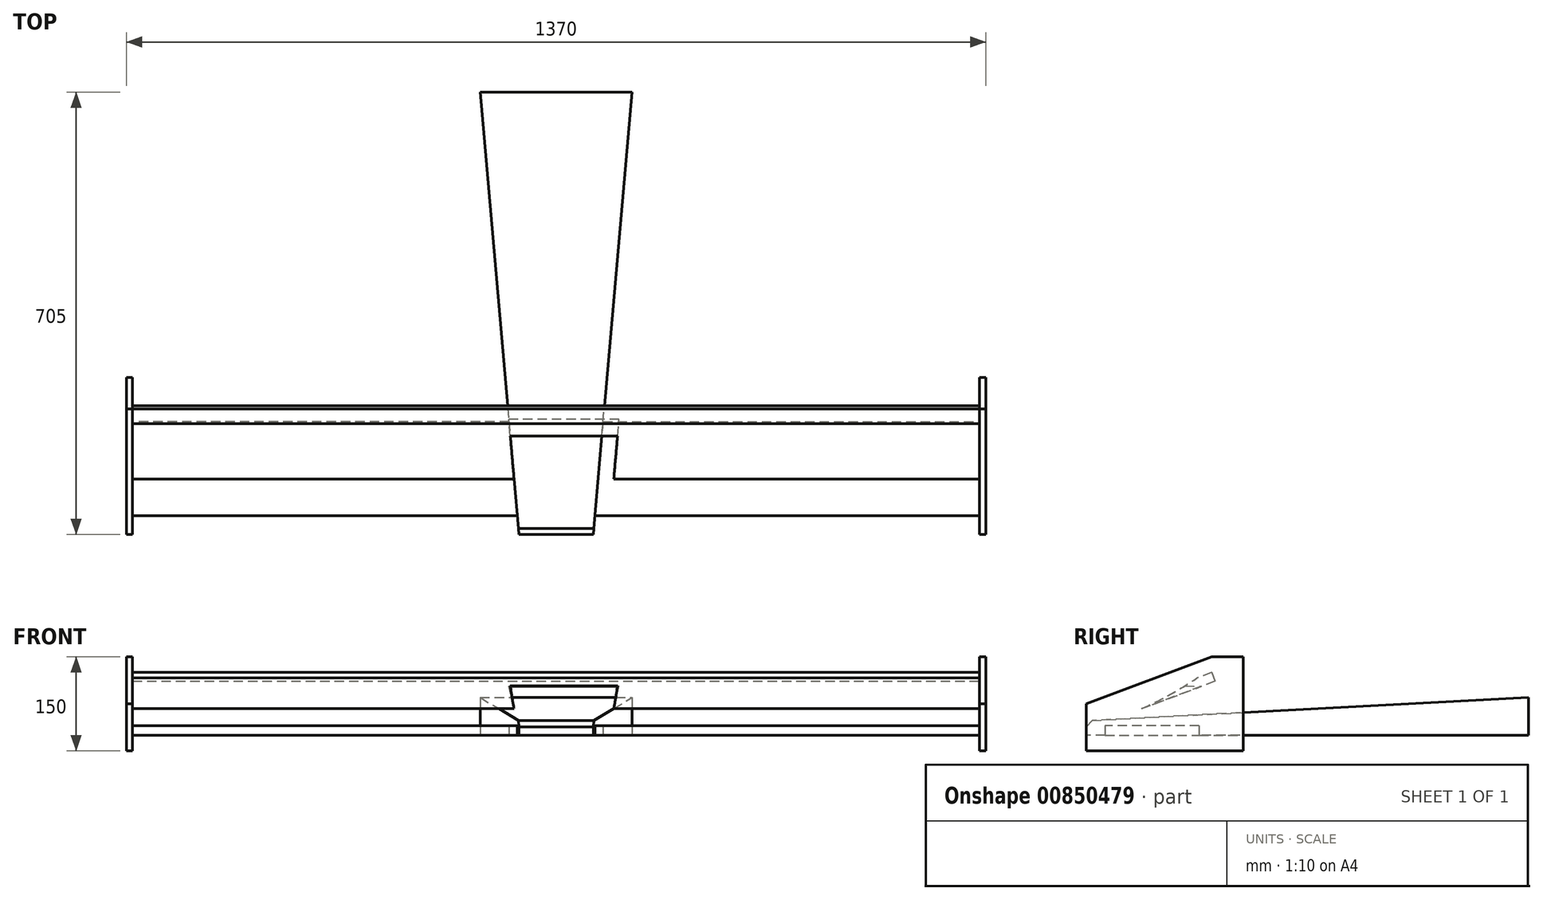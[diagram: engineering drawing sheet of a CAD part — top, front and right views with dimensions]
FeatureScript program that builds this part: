
annotation { "Feature Type Name" : "Feature", "Feature Type Description" : "" }
export const myFeature = defineFeature(function(context is Context, id is Id, definition is map)
    precondition{}
    {
        {
            var Q0;
            Q0=qCreatedBy(makeId("Top.planeOp"),FACE);
            var sketch = newSketch(context, id + "F0", { "sketchPlane" : qUnion([Q0])});
            skLineSegment(sketch, "E0", {"start": v(0, 0) * mm, "end": v(0, -525) * mm});
            skLineSegment(sketch, "E1", {"start": v(0, -525) * mm, "end": v(75, -525) * mm});
            skLineSegment(sketch, "E2", {"start": v(75, -525) * mm, "end": v(120.93, 0) * mm});
            skLineSegment(sketch, "E3", {"start": v(120.93, 0) * mm, "end": v(0, 0) * mm});
            skLineSegment(sketch, "E4", {"start": v(675, -675) * mm, "end": v(675, -525) * mm});
            skLineSegment(sketch, "E5", {"start": v(75, -525) * mm, "end": v(675, -525) * mm});
            skLineSegment(sketch, "E6", {"start": v(120.93, 0) * mm, "end": v(119.04, -21.63) * mm});
            skLineSegment(sketch, "E7", {"start": v(75, -525) * mm, "end": v(59.25, -705) * mm});
            skLineSegment(sketch, "E8", {"start": v(0, -525) * mm, "end": v(0, -705) * mm});
            skLineSegment(sketch, "E9", {"start": v(675, -675) * mm, "end": v(61.88, -675) * mm});
            skPoint(sketch, "E10", {"position": v(0, -675) * mm});
            skLineSegment(sketch, "E11", {"start": v(0, -705) * mm, "end": v(59.25, -705) * mm});
            skLineSegment(sketch, "E12", {"start": v(0, -877.72) * mm, "end": v(0, 311.7) * mm, "construction": true});
            skLineSegment(sketch, "E13.MirrorCS", {"start": v(-120.93, 0) * mm, "end": v(-119.04, -21.63) * mm});
            skLineSegment(sketch, "E14.MirrorCS", {"start": v(0, -705) * mm, "end": v(-59.25, -705) * mm});
            skLineSegment(sketch, "E15.MirrorCS", {"start": v(-75, -525) * mm, "end": v(-120.93, 0) * mm});
            skLineSegment(sketch, "E16.MirrorCS", {"start": v(-675, -675) * mm, "end": v(-61.88, -675) * mm});
            skLineSegment(sketch, "E17.MirrorCS", {"start": v(-75, -525) * mm, "end": v(-59.25, -705) * mm});
            skLineSegment(sketch, "E18.MirrorCS", {"start": v(0, -525) * mm, "end": v(-75, -525) * mm});
            skLineSegment(sketch, "E19.MirrorCS", {"start": v(-75, -525) * mm, "end": v(-675, -525) * mm});
            skLineSegment(sketch, "E20.MirrorCS", {"start": v(-120.93, 0) * mm, "end": v(0, 0) * mm});
            skLineSegment(sketch, "E21.MirrorCS", {"start": v(-675, -675) * mm, "end": v(-675, -525) * mm});
            skSolve(sketch);
        }
        {
            var Q0;
            {var subQ0=sQuery(id+"F0.wireOp",EDGE,"E16.MirrorCS");Q0=makeQuery(id+"F0.imprint","IMPRINT",FACE,{"disambiguationData":[TD([[makeQuery(id+"F0.imprint","IMPRINT",EDGE,{"derivedFrom":subQ0}),1.0]])]});}
            var Q1;
            {var subQ0=sQuery(id+"F0.wireOp",EDGE,"E18.MirrorCS");Q1=makeQuery(id+"F0.imprint","IMPRINT",FACE,{"disambiguationData":[TD([[makeQuery(id+"F0.imprint","IMPRINT",EDGE,{"derivedFrom":subQ0}),-1.0]])]});}
            var Q2;
            Q2=makeQuery(id+"F0.imprint","IMPRINT",FACE,{"disambiguationData":[TD([[makeQuery(id+"F0.imprint","IMPRINT",EDGE,{"derivedFrom":sQuery(id+"F0.wireOp",EDGE,"E1")}),1.0]])]});
            var Q3;
            {var subQ3=sQuery(id+"F0.wireOp",EDGE,"E14.MirrorCS");Q3=makeQuery(id+"F0.imprint","IMPRINT",FACE,{"disambiguationData":[TD([[makeQuery(id+"F0.imprint","IMPRINT",EDGE,{"derivedFrom":subQ3}),-1.0]])]});}
            var Q4;
            {var subQ3=sQuery(id+"F0.wireOp",EDGE,"E1");Q4=makeQuery(id+"F0.imprint","IMPRINT",FACE,{"disambiguationData":[TD([[makeQuery(id+"F0.imprint","IMPRINT",EDGE,{"derivedFrom":subQ3}),-1.0]])]});}
            var Q5;
            Q5=makeQuery(id+"F0.imprint","IMPRINT",FACE,{"disambiguationData":[TD([[makeQuery(id+"F0.imprint","IMPRINT",EDGE,{"derivedFrom":sQuery(id+"F0.wireOp",EDGE,"E4")}),1.0]])]});
            extrude(context, id + "F1", {"entities" : qUnion([Q0, Q1, Q2, Q3, Q4, Q5]), "depth" : 15 * mm, "offsetDistance" : 25 * mm});
        }
        {
            var Q0;
            Q0=makeQuery(id+"F1.opExtrude","SWEPT_FACE",FACE,{"disambiguationData":[OSD([sQuery(id+"F0.wireOp",EDGE,"E4")])]});
            var sketch = newSketch(context, id + "F2", { "sketchPlane" : qUnion([Q0])});
            skLineSegment(sketch, "E22.bottom", {"start": v(-675, 15) * mm, "end": v(-525, 15) * mm});
            skLineSegment(sketch, "E22.top", {"start": v(-675, 0) * mm, "end": v(-525, 0) * mm});
            skLineSegment(sketch, "E22.left", {"start": v(-675, 15) * mm, "end": v(-675, 0) * mm});
            skLineSegment(sketch, "E22.right", {"start": v(-525, 15) * mm, "end": v(-525, 0) * mm});
            skLineSegment(sketch, "E23", {"start": v(-705, 0) * mm, "end": v(-705, 50) * mm});
            skLineSegment(sketch, "E24", {"start": v(-705, 0) * mm, "end": v(-705, -25) * mm});
            skLineSegment(sketch, "E25", {"start": v(-705, -25) * mm, "end": v(-455, -25) * mm});
            skLineSegment(sketch, "E26", {"start": v(-455, -25) * mm, "end": v(-455, 125) * mm});
            skLineSegment(sketch, "E27", {"start": v(-455, 125) * mm, "end": v(-505, 125) * mm});
            skLineSegment(sketch, "E28", {"start": v(-705, 50) * mm, "end": v(-505, 125) * mm});
            skLineSegment(sketch, "E29.bottom", {"start": v(-705, 50) * mm, "end": v(-455, 50) * mm});
            skLineSegment(sketch, "E29.left", {"start": v(-705, 50) * mm, "end": v(-705, -25) * mm});
            skLineSegment(sketch, "E29.right", {"start": v(-455, 50) * mm, "end": v(-455, -25) * mm});
            skSolve(sketch);
        }
        {
            var Q0;
            Q0=makeQuery(id+"F2.imprint","IMPRINT",FACE,{"disambiguationData":[TD([[makeQuery(id+"F2.imprint","IMPRINT",EDGE,{"derivedFrom":sQuery(id+"F2.wireOp",EDGE,"E26")}),1.0]])]});
            var Q1;
            Q1=makeQuery(id+"F2.imprint","IMPRINT",FACE,{"disambiguationData":[TD([[makeQuery(id+"F2.imprint","IMPRINT",EDGE,{"derivedFrom":sQuery(id+"F2.wireOp",EDGE,"E22.bottom")}),1.0]])]});
            var Q2;
            Q2=makeQuery(id+"F2.imprint","IMPRINT",FACE,{"disambiguationData":[TD([[makeQuery(id+"F2.imprint","IMPRINT",EDGE,{"derivedFrom":sQuery(id+"F2.wireOp",EDGE,"E22.bottom")}),-1.0]])]});
            extrude(context, id + "F3", {"entities" : qUnion([Q0, Q1, Q2]), "operationType" : NewBodyOperationType.ADD, "depth" : 10 * mm, "offsetDistance" : 25 * mm});
        }
        {
            var Q0;
            Q0=makeQuery(id+"F1.opExtrude","SWEPT_FACE",FACE,{"disambiguationData":[OSD([sQuery(id+"F0.wireOp",EDGE,"E21.MirrorCS")])]});
            var sketch = newSketch(context, id + "F4", { "sketchPlane" : qUnion([Q0])});
            skLineSegment(sketch, "E30.bottom", {"start": v(525, 15) * mm, "end": v(675, 15) * mm});
            skLineSegment(sketch, "E30.top", {"start": v(525, 0) * mm, "end": v(675, 0) * mm});
            skLineSegment(sketch, "E30.left", {"start": v(525, 15) * mm, "end": v(525, 0) * mm});
            skLineSegment(sketch, "E30.right", {"start": v(675, 15) * mm, "end": v(675, 0) * mm});
            skLineSegment(sketch, "E31.bottom", {"start": v(455, 50) * mm, "end": v(705, 50) * mm});
            skLineSegment(sketch, "E31.top", {"start": v(455, -25) * mm, "end": v(705, -25) * mm});
            skLineSegment(sketch, "E31.left", {"start": v(455, 50) * mm, "end": v(455, -25) * mm});
            skLineSegment(sketch, "E31.right", {"start": v(705, 50) * mm, "end": v(705, -25) * mm});
            skLineSegment(sketch, "E32", {"start": v(455, 50) * mm, "end": v(455, 125) * mm});
            skLineSegment(sketch, "E33", {"start": v(455, 125) * mm, "end": v(505, 125) * mm});
            skLineSegment(sketch, "E34", {"start": v(705, 50) * mm, "end": v(505, 125) * mm});
            skSolve(sketch);
        }
        {
            var Q0;
            Q0 = qSketchRegion(id + "F4", true);
            var Q1;
            Q1=makeQuery(id+"F4.imprint","IMPRINT",FACE,{"disambiguationData":[TD([[makeQuery(id+"F4.imprint","IMPRINT",EDGE,{"derivedFrom":sQuery(id+"F4.wireOp",EDGE,"E30.bottom")}),1.0]])]});
            extrude(context, id + "F5", {"entities" : qUnion([Q0, Q1]), "depth" : 10 * mm, "offsetDistance" : 25 * mm});
        }
        {
            var Q0;
            Q0=makeQuery(id+"F1.opExtrude","CAP_FACE",FACE,{"disambiguationData":[OSD([sQuery(id+"F0.wireOp",EDGE,"E2"),sQuery(id+"F0.wireOp",EDGE,"E3"),sQuery(id+"F0.wireOp",EDGE,"E4"),sQuery(id+"F0.wireOp",EDGE,"E5"),sQuery(id+"F0.wireOp",EDGE,"E6"),sQuery(id+"F0.wireOp",EDGE,"E7"),sQuery(id+"F0.wireOp",EDGE,"E9"),sQuery(id+"F0.wireOp",EDGE,"E11"),sQuery(id+"F0.wireOp",EDGE,"E14.MirrorCS"),sQuery(id+"F0.wireOp",EDGE,"E15.MirrorCS"),sQuery(id+"F0.wireOp",EDGE,"E16.MirrorCS"),sQuery(id+"F0.wireOp",EDGE,"E17.MirrorCS"),sQuery(id+"F0.wireOp",EDGE,"E19.MirrorCS"),sQuery(id+"F0.wireOp",EDGE,"E20.MirrorCS"),sQuery(id+"F0.wireOp",EDGE,"E21.MirrorCS")])],"isStart":false});
            var sketch = newSketch(context, id + "F6", { "sketchPlane" : qUnion([Q0])});
            skLineSegment(sketch, "E35", {"start": v(-120.93, 0) * mm, "end": v(-59.25, -705) * mm});
            skLineSegment(sketch, "E36", {"start": v(-59.25, -705) * mm, "end": v(59.25, -705) * mm});
            skLineSegment(sketch, "E37", {"start": v(59.25, -705) * mm, "end": v(120.93, 0) * mm});
            skLineSegment(sketch, "E38", {"start": v(120.93, 0) * mm, "end": v(-120.93, 0) * mm});
            skSolve(sketch);
        }
        {
            var Q0;
            Q0 = qSketchRegion(id + "F6", true);
            extrude(context, id + "F7", {"entities" : qUnion([Q0]), "operationType" : NewBodyOperationType.ADD, "depth" : 45 * mm, "offsetDistance" : 25 * mm});
        }
        {
            var Q0;
            Q0=makeQuery(id+"F3.opExtrude","CAP_FACE",FACE,{"disambiguationData":[OSD([sQuery(id+"F2.wireOp",EDGE,"E26"),sQuery(id+"F2.wireOp",EDGE,"E27"),sQuery(id+"F2.wireOp",EDGE,"E28"),sQuery(id+"F2.wireOp",EDGE,"E25"),sQuery(id+"F2.wireOp",EDGE,"E29.left"),sQuery(id+"F2.wireOp",EDGE,"E29.right")])],"isStart":true});
            var sketch = newSketch(context, id + "F8", { "sketchPlane" : qUnion([Q0])});
            skLineSegment(sketch, "E39.bottom", {"start": v(455, 125) * mm, "end": v(705, 125) * mm, "construction": true});
            skLineSegment(sketch, "E39.top", {"start": v(455, -25) * mm, "end": v(705, -25) * mm, "construction": true});
            skLineSegment(sketch, "E39.left", {"start": v(455, 125) * mm, "end": v(455, -25) * mm, "construction": true});
            skLineSegment(sketch, "E39.right", {"start": v(705, 125) * mm, "end": v(705, -25) * mm, "construction": true});
            skLineSegment(sketch, "E40", {"start": v(505, 100.14) * mm, "end": v(528.4, 91.36) * mm});
            skLineSegment(sketch, "E41", {"start": v(505, 125) * mm, "end": v(705, 50) * mm, "construction": true});
            skLineSegment(sketch, "E42", {"start": v(505, 100.14) * mm, "end": v(499.73, 86.1) * mm});
            skLineSegment(sketch, "E43", {"start": v(499.73, 86.1) * mm, "end": v(616.77, 42.2) * mm});
            skArc(sketch, "E44", {"start": v(528.4, 91.36) * mm, "mid": v(571.55, 64.92) * mm, "end": v(616.77, 42.2) * mm});
            skSolve(sketch);
        }
        {
            var Q0;
            Q0=makeQuery(id+"F8.imprint","IMPRINT",FACE,{"disambiguationData":[TD([[makeQuery(id+"F8.imprint","IMPRINT",EDGE,{"derivedFrom":sQuery(id+"F8.wireOp",EDGE,"E42")}),1.0]])]});
            var Q1;
            Q1=makeQuery(id+"F5.opExtrude","CAP_FACE",FACE,{"disambiguationData":[OSD([sQuery(id+"F4.wireOp",EDGE,"E31.top"),sQuery(id+"F4.wireOp",EDGE,"E31.left"),sQuery(id+"F4.wireOp",EDGE,"E31.right"),sQuery(id+"F4.wireOp",EDGE,"E32"),sQuery(id+"F4.wireOp",EDGE,"E33"),sQuery(id+"F4.wireOp",EDGE,"E34")])],"isStart":true});
            extrude(context, id + "F9", {"entities" : qUnion([Q0]), "endBound" : BoundingType.UP_TO_SURFACE, "depth" : 25 * mm, "endBoundEntityFace" : qUnion([Q1]), "offsetDistance" : 25 * mm});
        }
        {
            var Q0;
            Q0=qCreatedBy(makeId("Right.planeOp"),FACE);
            var sketch = newSketch(context, id + "F10", { "sketchPlane" : qUnion([Q0])});
            skLineSegment(sketch, "E45.left", {"start": v(0, 0) * mm, "end": v(0, 60) * mm});
            skPoint(sketch, "E46.orphan", {"position": v(0, -8.34) * mm});
            skLineSegment(sketch, "E47", {"start": v(0, 0) * mm, "end": v(-705.38, 0) * mm});
            skLineSegment(sketch, "E48", {"start": v(0, 60) * mm, "end": v(-826.11, 16.7) * mm});
            skLineSegment(sketch, "E49", {"start": v(-826.11, 16.7) * mm, "end": v(-825.24, 0) * mm});
            skLineSegment(sketch, "E50", {"start": v(-825.24, 0) * mm, "end": v(-705.38, 0) * mm});
            skLineSegment(sketch, "E51", {"start": v(-826.11, 16.7) * mm, "end": v(-829.88, 88.52) * mm});
            skLineSegment(sketch, "E52", {"start": v(-829.88, 88.52) * mm, "end": v(0, 60) * mm});
            skSolve(sketch);
        }
        {
            var Q0;
            Q0=makeQuery(id+"F10.imprint","IMPRINT",FACE,{"disambiguationData":[TD([[makeQuery(id+"F10.imprint","IMPRINT",EDGE,{"derivedFrom":sQuery(id+"F10.wireOp",EDGE,"E48")}),-1.0]])]});
            var Q1;
            Q1=makeQuery(id+"F7.boolean.opBoolean","MERGE",FACE,{"derivedFrom":[makeQuery(id+"F1.opExtrude","SWEPT_FACE",FACE,{"disambiguationData":[OSD([sQuery(id+"F0.wireOp",EDGE,"E2"),sQuery(id+"F0.wireOp",EDGE,"E6")])]}),makeQuery(id+"F1.opExtrude","SWEPT_FACE",FACE,{"disambiguationData":[OSD([sQuery(id+"F0.wireOp",EDGE,"E7")])]}),makeQuery(id+"F7.opExtrude","SWEPT_FACE",FACE,{"disambiguationData":[OSD([sQuery(id+"F6.wireOp",EDGE,"E37")])]})]});
            var Q2;
            Q2=makeQuery(id+"F7.boolean.opBoolean","MERGE",FACE,{"derivedFrom":[makeQuery(id+"F1.opExtrude","SWEPT_FACE",FACE,{"disambiguationData":[OSD([sQuery(id+"F0.wireOp",EDGE,"E15.MirrorCS")])]}),makeQuery(id+"F1.opExtrude","SWEPT_FACE",FACE,{"disambiguationData":[OSD([sQuery(id+"F0.wireOp",EDGE,"E17.MirrorCS")])]}),makeQuery(id+"F7.opExtrude","SWEPT_FACE",FACE,{"disambiguationData":[OSD([sQuery(id+"F6.wireOp",EDGE,"E35")])]})]});
            extrude(context, id + "F11", {"entities" : qUnion([Q0]), "operationType" : NewBodyOperationType.REMOVE, "endBound" : BoundingType.UP_TO_SURFACE, "depth" : 25 * mm, "endBoundEntityFace" : qUnion([Q1]), "hasOffset" : true, "offsetDistance" : 25 * mm, "offsetOppositeDirection" : true, "hasSecondDirection" : true, "secondDirectionBound" : SecondDirectionBoundingType.UP_TO_SURFACE, "secondDirectionOppositeDirection" : true, "secondDirectionDepth" : 25 * mm, "secondDirectionBoundEntityFace" : qUnion([Q2])});
        }
        {
            var Q0;
            Q0=makeQuery(id+"F11.boolean.opBoolean","INTERSECT",EDGE,{"derivedFrom":[makeQuery(id+"F7.boolean.opBoolean","MERGE",FACE,{"derivedFrom":[makeQuery(id+"F1.opExtrude","SWEPT_FACE",FACE,{"disambiguationData":[OSD([sQuery(id+"F0.wireOp",EDGE,"E11"),sQuery(id+"F0.wireOp",EDGE,"E14.MirrorCS")])]}),makeQuery(id+"F7.opExtrude","SWEPT_FACE",FACE,{"disambiguationData":[OSD([sQuery(id+"F6.wireOp",EDGE,"E36")])]})]}),makeQuery(id+"F11.opExtrude","SWEPT_FACE",FACE,{"disambiguationData":[OSD([sQuery(id+"F10.wireOp",EDGE,"E48")])]})]});
            chamfer(context, id + "F12", {"entities" : qUnion([Q0]), "width" : 10 * mm, "tangentPropagation" : true});
        }
    });
